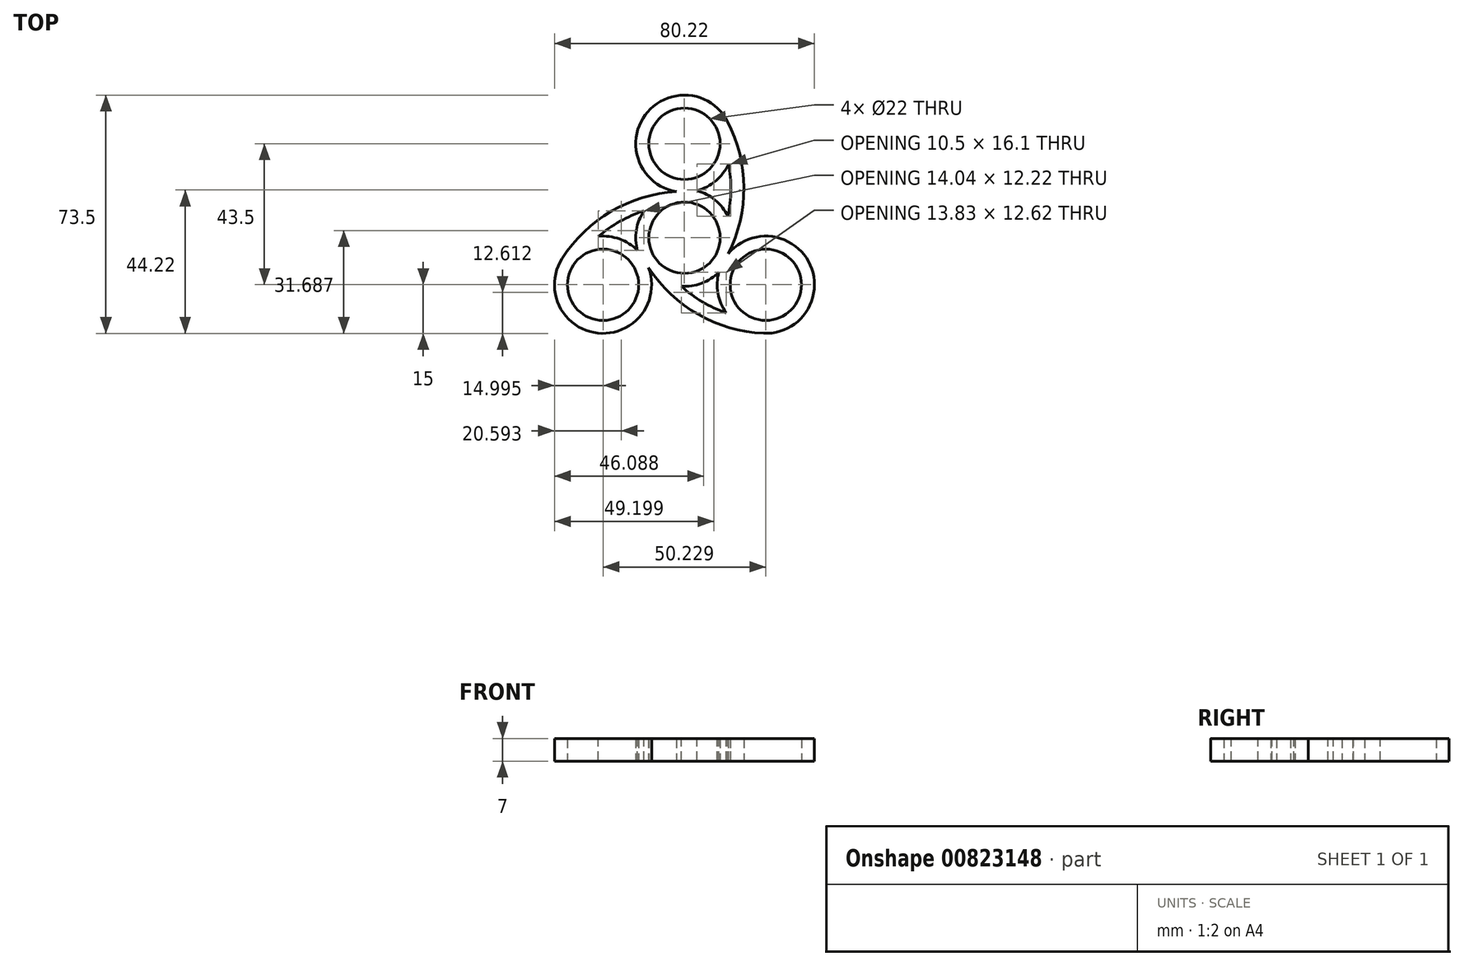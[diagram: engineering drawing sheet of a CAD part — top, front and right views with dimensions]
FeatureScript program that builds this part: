
annotation { "Feature Type Name" : "Feature", "Feature Type Description" : "" }
export const myFeature = defineFeature(function(context is Context, id is Id, definition is map)
    precondition{}
    {
        {
            var Q0;
            Q0=qCreatedBy(makeId("Top.planeOp"),FACE);
            var sketch = newSketch(context, id + "F0", { "sketchPlane" : qUnion([Q0])});
            skCircle(sketch, "E0", {"center": v(0, 0) * mm, "radius": 11 * mm});
            skCircle(sketch, "E1", {"center": v(0, 0) * mm, "radius": 43 * mm, "construction": true});
            skLineSegment(sketch, "E2", {"start": v(0, 0) * mm, "end": v(0, 43) * mm, "construction": true});
            skLineSegment(sketch, "E3", {"start": v(0, 0) * mm, "end": v(-37.24, -21.5) * mm, "construction": true});
            skLineSegment(sketch, "E4", {"start": v(0, 0) * mm, "end": v(37.24, -21.5) * mm, "construction": true});
            skCircle(sketch, "E5", {"center": v(0, 29) * mm, "radius": 11 * mm});
            skCircle(sketch, "E6", {"center": v(25.11, -14.5) * mm, "radius": 11 * mm});
            skCircle(sketch, "E7", {"center": v(-25.11, -14.5) * mm, "radius": 11 * mm});
            skCircle(sketch, "E8", {"center": v(0, 0) * mm, "radius": 29 * mm, "construction": true});
            skArc(sketch, "E9", {"start": v(-2.52, 14.21) * mm, "mid": v(-22.6, 8.13) * mm, "end": v(-37.74, -6.4) * mm});
            skArc(sketch, "E10", {"start": v(-37.74, -6.4) * mm, "mid": v(-26.73, -29.41) * mm, "end": v(-11.05, -9.29) * mm});
            skArc(sketch, "E11", {"start": v(-11.05, -9.29) * mm, "mid": v(4.26, -23.63) * mm, "end": v(24.4, -29.48) * mm});
            skArc(sketch, "E12", {"start": v(24.4, -29.48) * mm, "mid": v(38.84, -8.44) * mm, "end": v(13.57, -4.93) * mm});
            skArc(sketch, "E13", {"start": v(13.57, -4.93) * mm, "mid": v(18.34, 15.5) * mm, "end": v(13.33, 35.88) * mm});
            skArc(sketch, "E14", {"start": v(13.33, 35.88) * mm, "mid": v(-12.1, 37.86) * mm, "end": v(-2.52, 14.21) * mm});
            skLineSegment(sketch, "E15", {"start": v(-2.52, 14.21) * mm, "end": v(13.57, -4.93) * mm, "construction": true});
            skLineSegment(sketch, "E16", {"start": v(13.57, -4.93) * mm, "end": v(-11.05, -9.29) * mm, "construction": true});
            skLineSegment(sketch, "E17", {"start": v(-11.05, -9.29) * mm, "end": v(-2.52, 14.21) * mm, "construction": true});
            skSolve(sketch);
        }
        {
            var Q0;
            Q0=qSketchRegion(id+"F0",true);
            extrude(context, id + "F1", {"entities" : qUnion([Q0]), "depth" : 7 * mm, "offsetDistance" : 25 * mm});
        }
        {
            var Q0;
            Q0=makeQuery(id+"F1.opExtrude","CAP_FACE",FACE,{"disambiguationData":[OSD([sQuery(id+"F0.wireOp",EDGE,"E0"),sQuery(id+"F0.wireOp",EDGE,"E5"),sQuery(id+"F0.wireOp",EDGE,"E6"),sQuery(id+"F0.wireOp",EDGE,"E7"),sQuery(id+"F0.wireOp",EDGE,"E9"),sQuery(id+"F0.wireOp",EDGE,"E10"),sQuery(id+"F0.wireOp",EDGE,"E11"),sQuery(id+"F0.wireOp",EDGE,"E12"),sQuery(id+"F0.wireOp",EDGE,"E13"),sQuery(id+"F0.wireOp",EDGE,"E14")])],"isStart":false});
            var sketch = newSketch(context, id + "F2", { "sketchPlane" : qUnion([Q0])});
            skArc(sketch, "E18", {"start": v(3.84, 14.5) * mm, "mid": v(9.67, 17.53) * mm, "end": v(13.64, 22.77) * mm});
            skArc(sketch, "E19", {"start": v(13.43, 6.67) * mm, "mid": v(14.34, 14.7) * mm, "end": v(13.64, 22.77) * mm});
            skArc(sketch, "E20", {"start": v(13.43, 6.67) * mm, "mid": v(9.48, 11.62) * mm, "end": v(3.84, 14.5) * mm});
            skLineSegment(sketch, "E21", {"start": v(9.67, 17.53) * mm, "end": v(0, 29) * mm, "construction": true});
            skLineSegment(sketch, "E22", {"start": v(9.48, 11.62) * mm, "end": v(0, 0) * mm, "construction": true});
            skArc(sketch, "E23.1.0", {"start": v(-12.5, 8.3) * mm, "mid": v(-14.8, 2.4) * mm, "end": v(-14.48, -3.92) * mm});
            skLineSegment(sketch, "E23.1.1", {"start": v(-20.02, -0.4) * mm, "end": v(-25.11, -14.5) * mm, "construction": true});
            skArc(sketch, "E23.1.2", {"start": v(-12.5, 8.3) * mm, "mid": v(-19.9, 5.06) * mm, "end": v(-26.54, 0.43) * mm});
            skArc(sketch, "E23.1.3", {"start": v(-14.48, -3.92) * mm, "mid": v(-20.02, -0.4) * mm, "end": v(-26.54, 0.43) * mm});
            skArc(sketch, "E23.2.0", {"start": v(-0.94, -14.97) * mm, "mid": v(5.32, -14.02) * mm, "end": v(10.64, -10.58) * mm});
            skLineSegment(sketch, "E23.2.1", {"start": v(10.35, -17.14) * mm, "end": v(25.11, -14.5) * mm, "construction": true});
            skArc(sketch, "E23.2.2", {"start": v(-0.94, -14.97) * mm, "mid": v(5.57, -19.77) * mm, "end": v(12.9, -23.2) * mm});
            skArc(sketch, "E23.2.3", {"start": v(10.64, -10.58) * mm, "mid": v(10.35, -17.14) * mm, "end": v(12.9, -23.2) * mm});
            skSolve(sketch);
        }
        {
            var Q0;
            Q0=qSketchRegion(id+"F2",true);
            extrude(context, id + "F3", {"entities" : qUnion([Q0]), "operationType" : NewBodyOperationType.REMOVE, "oppositeDirection" : true, "depth" : 25 * mm, "offsetDistance" : 25 * mm});
        }
    });
